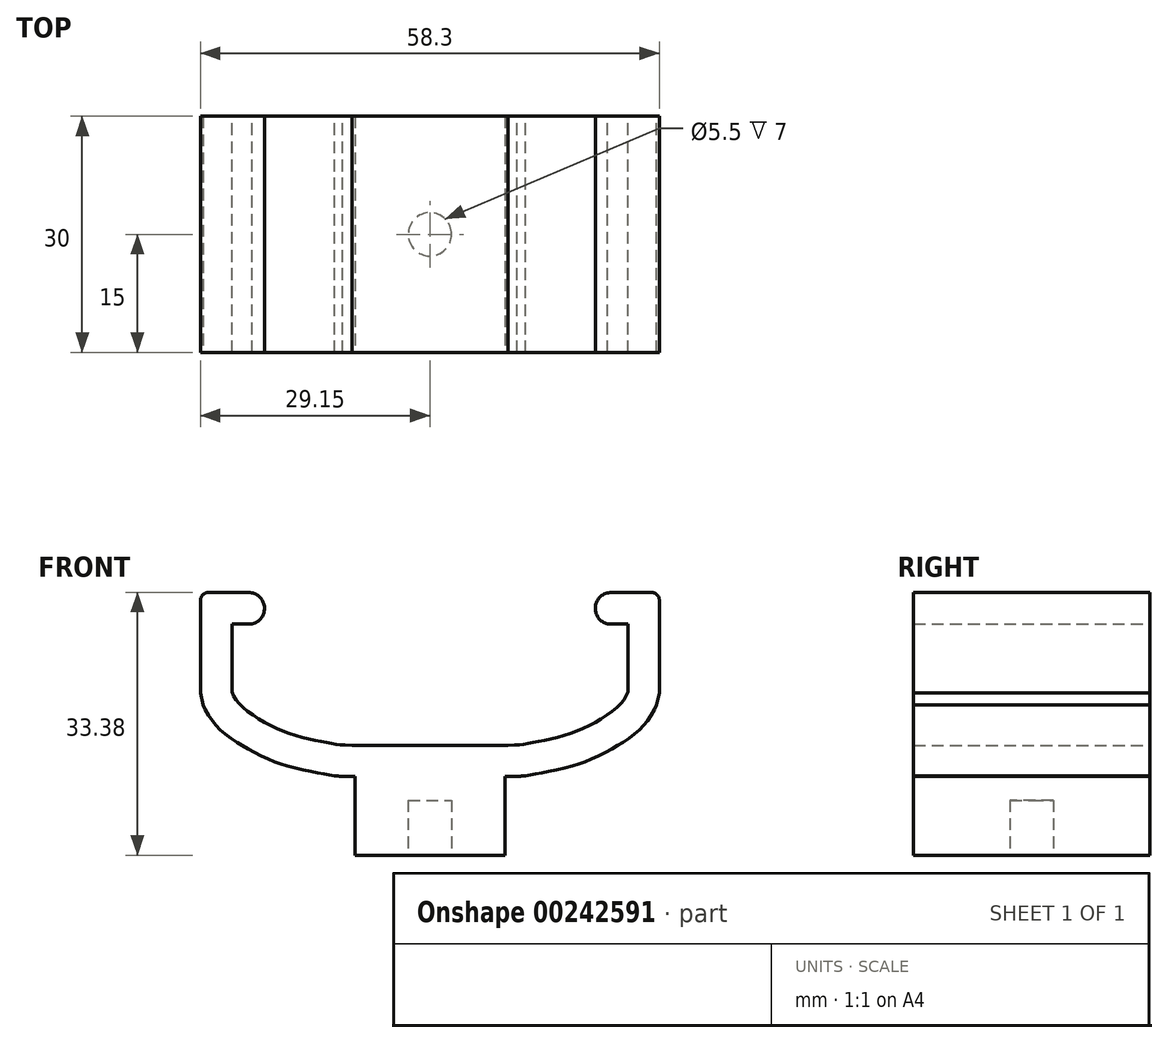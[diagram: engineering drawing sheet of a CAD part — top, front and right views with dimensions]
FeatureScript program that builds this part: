
annotation { "Feature Type Name" : "Feature", "Feature Type Description" : "" }
export const myFeature = defineFeature(function(context is Context, id is Id, definition is map)
    precondition{}
    {
        {
            var Q0;
            Q0=qCreatedBy(makeId("Front.planeOp"),FACE);
            var sketch = newSketch(context, id + "F0", { "sketchPlane" : qUnion([Q0])});
            skLineSegment(sketch, "E0.2", {"start": v(29.15, 0) * mm, "end": v(29.15, -8.78) * mm});
            skLineSegment(sketch, "E1", {"start": v(29.15, 0) * mm, "end": v(29.15, 3) * mm});
            skLineSegment(sketch, "E2", {"start": v(22.58, 0) * mm, "end": v(25.15, 0) * mm});
            skLineSegment(sketch, "E3", {"start": v(23.04, 4) * mm, "end": v(28.15, 4) * mm});
            skArc(sketch, "E4", {"start": v(23.04, 4) * mm, "mid": v(21.02, 2.2) * mm, "end": v(22.58, 0) * mm});
            skPoint(sketch, "E5.visualSharp", {"position": v(29.15, 4) * mm});
            skArc(sketch, "E5.filletArc", {"start": v(29.15, 3) * mm, "mid": v(28.86, 3.7) * mm, "end": v(28.15, 4) * mm});
            skLineSegment(sketch, "E6", {"start": v(25.15, 0) * mm, "end": v(25.15, -8.63) * mm});
            skFitSpline(sketch, "E7", {"points": [v(25.15, -8.63) * mm, v(24.26, -10.12) * mm, v(21.68, -12.09) * mm, v(18.22, -13.79) * mm, v(14.6, -14.77) * mm, v(12.12, -15.24) * mm, v(9.9, -15.4) * mm], "startDerivative": vector(-5.24, -11.48) * mm, "endDerivative": vector(-23.57, 0.36) * mm});
            skLineSegment(sketch, "E8", {"start": v(9.9, -15.4) * mm, "end": v(0, -15.4) * mm});
            skLineSegment(sketch, "E9", {"start": v(0, -15.4) * mm, "end": v(0, -19.38) * mm});
            skFitSpline(sketch, "E10.0", {"points": [v(28.79, -10.29) * mm, v(28.73, -10.4) * mm, v(28.6, -10.7) * mm, v(28.32, -11.26) * mm, v(28, -11.81) * mm, v(27.66, -12.28) * mm, v(27.38, -12.63) * mm, v(27.07, -12.98) * mm, v(26.77, -13.29) * mm, v(26.46, -13.58) * mm, v(26.04, -13.93) * mm, v(25.53, -14.34) * mm, v(24.9, -14.77) * mm, v(24.39, -15.11) * mm, v(23.98, -15.37) * mm, v(23.58, -15.61) * mm, v(23.06, -15.91) * mm, v(22.43, -16.26) * mm, v(21.78, -16.6) * mm, v(21.1, -16.93) * mm, v(20.4, -17.23) * mm, v(19.8, -17.47) * mm, v(19.31, -17.65) * mm, v(18.83, -17.81) * mm, v(18.23, -18) * mm, v(17.53, -18.2) * mm, v(16.62, -18.43) * mm, v(15.76, -18.62) * mm, v(14.96, -18.78) * mm, v(14.39, -18.9) * mm, v(13.85, -19) * mm, v(13.35, -19.08) * mm, v(12.97, -19.15) * mm, v(12.7, -19.2) * mm, v(12.4, -19.24) * mm, v(11.95, -19.31) * mm, v(11.32, -19.37) * mm, v(10.63, -19.4) * mm, v(10.12, -19.4) * mm, v(9.84, -19.4) * mm]});
            skFitSpline(sketch, "E11", {"points": [v(29.15, -8.78) * mm, v(28.79, -10.29) * mm], "startDerivative": vector(-0.36, -1.5) * mm, "endDerivative": vector(-0.36, -1.5) * mm});
            skLineSegment(sketch, "E12", {"start": v(9.54, -19.38) * mm, "end": v(0, -19.38) * mm});
            skFitSpline(sketch, "E13", {"points": [v(11.09, -19.38) * mm, v(9.54, -19.38) * mm], "startDerivative": vector(-1.55, 0) * mm, "endDerivative": vector(-1.55, 0) * mm});
            skFitSpline(sketch, "E14", {"points": [v(11.09, -19.38) * mm, v(12.24, -19.27) * mm], "startDerivative": vector(1.15, 0.14) * mm, "endDerivative": vector(1.15, 0.14) * mm});
            skSolve(sketch);
        }
        {
            var Q0;
            Q0 = qSketchRegion(id + "F0", true);
            extrude(context, id + "F1", {"entities" : qUnion([Q0]), "depth" : 30 * mm});
        }
        {
            var Q0;
            Q0=makeQuery(id+"F1.opExtrude","SWEPT_FACE",FACE,{"disambiguationData":[OSD([sQuery(id+"F0.wireOp",EDGE,"E12")])]});
            var sketch = newSketch(context, id + "F2", { "sketchPlane" : qUnion([Q0])});
            skLineSegment(sketch, "E15.bottom", {"start": v(0, 0) * mm, "end": v(9.54, 0) * mm});
            skLineSegment(sketch, "E15.top", {"start": v(0, 30) * mm, "end": v(9.54, 30) * mm});
            skLineSegment(sketch, "E15.left", {"start": v(0, 0) * mm, "end": v(0, 30) * mm});
            skLineSegment(sketch, "E15.right", {"start": v(9.54, 0) * mm, "end": v(9.54, 30) * mm});
            skSolve(sketch);
        }
        {
            var Q0;
            Q0 = qSketchRegion(id + "F2", true);
            extrude(context, id + "F3", {"entities" : qUnion([Q0]), "operationType" : NewBodyOperationType.ADD, "depth" : 10 * mm});
        }
        {
            var Q0;
            Q0=makeQuery(id+"F1.opExtrude","SWEPT_BODY",BODY,{"disambiguationData":[OSD([sQuery(id+"F0.wireOp",EDGE,"uN4nS8UW-hTzL-3zEq-UgDd-DzXpN1DiGHEj"),sQuery(id+"F0.wireOp",EDGE,"5vrN7j9X-sG0m-kto4-DH6V-177vufrbckWc"),sQuery(id+"F0.wireOp",EDGE,"014af4e0-9e4b-4937-a52f-1dcfb5b7689f"),sQuery(id+"F0.wireOp",EDGE,"E0.0"),sQuery(id+"F0.wireOp",EDGE,"E0.1"),sQuery(id+"F0.wireOp",EDGE,"E0.2"),sQuery(id+"F0.wireOp",EDGE,"E1"),sQuery(id+"F0.wireOp",EDGE,"E2"),sQuery(id+"F0.wireOp",EDGE,"E3"),sQuery(id+"F0.wireOp",EDGE,"YHYGd0Hi-nQTi-RF2R-H9qn-tA1pWZFsSvje"),sQuery(id+"F0.wireOp",EDGE,"E4"),sQuery(id+"F0.wireOp",EDGE,"E5.filletArc")])]});
            var Q1;
            Q1=qCreatedBy(makeId("Right.planeOp"),FACE);
            mirror(context, id + "F4", {"operationType" : NewBodyOperationType.ADD, "entities" : qUnion([Q0]), "mirrorPlane" : qUnion([Q1])});
        }
        {
            var Q0;
            Q0=makeQuery(id+"F3.opExtrude","CAP_FACE",FACE,{"disambiguationData":[OSD([sQuery(id+"F2.wireOp",EDGE,"E15.bottom"),sQuery(id+"F2.wireOp",EDGE,"E15.top"),sQuery(id+"F2.wireOp",EDGE,"E15.left"),sQuery(id+"F2.wireOp",EDGE,"E15.right")])],"isStart":false});
            var sketch = newSketch(context, id + "F5", { "sketchPlane" : qUnion([Q0])});
            skCircle(sketch, "E16", {"center": v(0, 15) * mm, "radius": 2.75 * mm});
            skSolve(sketch);
        }
        {
            var Q0;
            Q0 = qSketchRegion(id + "F5", true);
            extrude(context, id + "F6", {"entities" : qUnion([Q0]), "operationType" : NewBodyOperationType.REMOVE, "oppositeDirection" : true, "depth" : 7 * mm});
        }
    });
